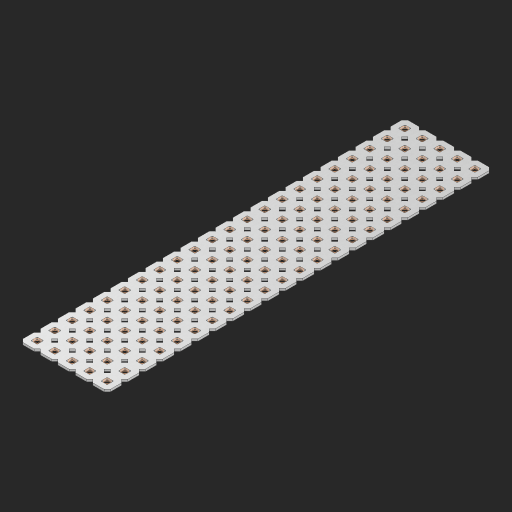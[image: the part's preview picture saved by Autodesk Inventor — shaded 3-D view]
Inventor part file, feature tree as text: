
AUTODESK INVENTOR PART (.ipt)
format: ipt  version: 2023 (Build 270158000, 158)  size: 1,554,432 bytes
history: native  units: in
note: dims shown in document units (in); Inventor stores cm internally (conversion verified against a paired STEP export)
features: other x111, extrude x109, sketch x2, pattern_linear x1
ambient origin geometry x8: Origin, YZ Plane, XZ Plane, XY Plane, X Axis, Y Axis, Z Axis, Center Point
bodies: Solid1 (feature_tree), Body (feature_tree)
feature tree (223):
  pattern_linear  "Rectangular Pattern1"  Spacing1=0.09in  [1 undecoded]
  sketch  "Sketch1"  dims[d1=0.5in]
  sketch  "Sketch2"  dims[d2=0.182in d3=0.09in d4=0.09in d5=0.09in d6=0.09in d7=0.09in d8=0.09in d9=0.09in d10=0.09in d11=0.02in d13=0.0in d14=0.172in d15=0.0625in d16=0.0in d19=0.5in d22=0.5in]
  other  "Srf1"
  other  "Srf126"
  other  "Srf127"
  other  "Srf128"
  other  "Srf129"
  other  "Srf130"
  other  "Srf131"
  other  "Srf250"
  other  "Srf251"
  other  "Srf252"
  other  "Srf253"
  other  "Srf254"
  other  "Srf255"
  other  "Srf256"
  other  "Srf257"
  other  "Srf258"
  other  "Srf259"
  other  "Srf260"
  other  "Srf261"
  other  "Srf262"
  other  "Srf263"
  other  "Srf264"
  other  "Srf268"
  other  "Srf269"
  other  "Srf270"
  other  "Srf271"
  other  "Srf272"
  other  "Srf273"
  other  "Srf274"
  other  "Srf275"
  other  "Srf276"
  other  "Srf277"
  other  "Srf278"
  other  "Srf279"
  other  "Srf280"
  other  "Srf281"
  other  "Srf282"
  other  "Srf283"
  other  "Srf284"
  other  "Srf285"
  other  "Srf286"
  other  "Srf287"
  other  "Srf288"
  other  "Srf289"
  other  "Srf293"
  other  "Srf294"
  other  "Srf295"
  other  "Srf296"
  other  "Srf297"
  other  "Srf298"
  other  "Srf299"
  other  "Srf300"
  other  "Srf301"
  other  "Srf302"
  other  "Srf303"
  other  "Srf304"
  other  "Srf305"
  other  "Srf306"
  other  "Srf307"
  other  "Srf308"
  other  "Srf309"
  other  "Srf310"
  other  "Srf311"
  other  "Srf312"
  other  "Srf313"
  other  "Srf314"
  other  "Srf318"
  other  "Srf319"
  other  "Srf320"
  other  "Srf321"
  other  "Srf322"
  other  "Srf323"
  other  "Srf324"
  other  "Srf325"
  other  "Srf326"
  other  "Srf327"
  other  "Srf328"
  other  "Srf329"
  other  "Srf330"
  other  "Srf331"
  other  "Srf332"
  other  "Srf333"
  other  "Srf334"
  other  "Srf335"
  other  "Srf336"
  other  "Srf337"
  other  "Srf338"
  other  "Srf339"
  other  "Srf343"
  other  "Srf344"
  other  "Srf345"
  other  "Srf346"
  other  "Srf347"
  other  "Srf348"
  other  "Srf349"
  other  "Srf350"
  other  "Srf351"
  other  "Srf352"
  other  "Srf353"
  other  "Srf354"
  other  "Srf355"
  other  "Srf356"
  other  "Srf357"
  other  "Srf358"
  other  "Srf359"
  other  "Srf360"
  other  "Srf361"
  other  "Srf362"
  other  "Srf363"
  other  "Srf364"
  other  "Circle"
  extrude  "ExtrusionSrf126"  Depth=0.09in
  extrude  "ExtrusionSrf127"  Depth=0.09in
  extrude  "ExtrusionSrf128"  Depth=0.09in
  extrude  "ExtrusionSrf129"  Depth=0.09in
  extrude  "ExtrusionSrf130"  Depth=0.09in
  extrude  "ExtrusionSrf131"  Depth=0.09in
  extrude  "ExtrusionSrf250"  Depth=0.09in
  extrude  "ExtrusionSrf251"  Depth=0.02in
  extrude  "ExtrusionSrf252"  TaperAngle=0.0deg  [1 undecoded]
  extrude  "ExtrusionSrf253"  Depth=0.5in
  extrude  "ExtrusionSrf254"  Depth=0.0625in TaperAngle=0.0deg
  extrude  "ExtrusionSrf255"  Depth=0.5in
  extrude  "ExtrusionSrf256"  Depth=0.5in
  extrude  "ExtrusionSrf257"  [1 undecoded]
  extrude  "ExtrusionSrf258"  [1 undecoded]
  extrude  "ExtrusionSrf259"  [1 undecoded]
  extrude  "ExtrusionSrf260"  [1 undecoded]
  extrude  "ExtrusionSrf261"  [1 undecoded]
  extrude  "ExtrusionSrf262"  [1 undecoded]
  extrude  "ExtrusionSrf263"  [1 undecoded]
  extrude  "ExtrusionSrf264"  [1 undecoded]
  extrude  "ExtrusionSrf268"  [1 undecoded]
  extrude  "ExtrusionSrf269"  [1 undecoded]
  extrude  "ExtrusionSrf270"  [1 undecoded]
  extrude  "ExtrusionSrf271"  [1 undecoded]
  extrude  "ExtrusionSrf272"  [1 undecoded]
  extrude  "ExtrusionSrf273"  [1 undecoded]
  extrude  "ExtrusionSrf274"  [1 undecoded]
  extrude  "ExtrusionSrf275"  [1 undecoded]
  extrude  "ExtrusionSrf276"  [1 undecoded]
  extrude  "ExtrusionSrf277"  [1 undecoded]
  extrude  "ExtrusionSrf278"  [1 undecoded]
  extrude  "ExtrusionSrf279"  [1 undecoded]
  extrude  "ExtrusionSrf280"  [1 undecoded]
  extrude  "ExtrusionSrf281"  [1 undecoded]
  extrude  "ExtrusionSrf282"  [1 undecoded]
  extrude  "ExtrusionSrf283"  [1 undecoded]
  extrude  "ExtrusionSrf284"  [1 undecoded]
  extrude  "ExtrusionSrf285"  [1 undecoded]
  extrude  "ExtrusionSrf286"  [1 undecoded]
  extrude  "ExtrusionSrf287"  [1 undecoded]
  extrude  "ExtrusionSrf288"  [1 undecoded]
  extrude  "ExtrusionSrf289"  [1 undecoded]
  extrude  "ExtrusionSrf293"  [1 undecoded]
  extrude  "ExtrusionSrf294"  [1 undecoded]
  extrude  "ExtrusionSrf295"  [1 undecoded]
  extrude  "ExtrusionSrf296"  [1 undecoded]
  extrude  "ExtrusionSrf297"  [1 undecoded]
  extrude  "ExtrusionSrf298"  [1 undecoded]
  extrude  "ExtrusionSrf299"  [1 undecoded]
  extrude  "ExtrusionSrf300"  [1 undecoded]
  extrude  "ExtrusionSrf301"  [1 undecoded]
  extrude  "ExtrusionSrf302"  [1 undecoded]
  extrude  "ExtrusionSrf303"  [1 undecoded]
  extrude  "ExtrusionSrf304"  [1 undecoded]
  extrude  "ExtrusionSrf305"  [1 undecoded]
  extrude  "ExtrusionSrf306"  [1 undecoded]
  extrude  "ExtrusionSrf307"  [1 undecoded]
  extrude  "ExtrusionSrf308"  [1 undecoded]
  extrude  "ExtrusionSrf309"  [1 undecoded]
  extrude  "ExtrusionSrf310"  [1 undecoded]
  extrude  "ExtrusionSrf311"  [1 undecoded]
  extrude  "ExtrusionSrf312"  [1 undecoded]
  extrude  "ExtrusionSrf313"  [1 undecoded]
  extrude  "ExtrusionSrf314"  [1 undecoded]
  extrude  "ExtrusionSrf318"  [1 undecoded]
  extrude  "ExtrusionSrf319"  [1 undecoded]
  extrude  "ExtrusionSrf320"  [1 undecoded]
  extrude  "ExtrusionSrf321"  [1 undecoded]
  extrude  "ExtrusionSrf322"  [1 undecoded]
  extrude  "ExtrusionSrf323"  [1 undecoded]
  extrude  "ExtrusionSrf324"  [1 undecoded]
  extrude  "ExtrusionSrf325"  [1 undecoded]
  extrude  "ExtrusionSrf326"  [1 undecoded]
  extrude  "ExtrusionSrf327"  [1 undecoded]
  extrude  "ExtrusionSrf328"  [1 undecoded]
  extrude  "ExtrusionSrf329"  [1 undecoded]
  extrude  "ExtrusionSrf330"  [1 undecoded]
  extrude  "ExtrusionSrf331"  [1 undecoded]
  extrude  "ExtrusionSrf332"  [1 undecoded]
  extrude  "ExtrusionSrf333"  [1 undecoded]
  extrude  "ExtrusionSrf334"  [1 undecoded]
  extrude  "ExtrusionSrf335"  [1 undecoded]
  extrude  "ExtrusionSrf336"  [1 undecoded]
  extrude  "ExtrusionSrf337"  [1 undecoded]
  extrude  "ExtrusionSrf338"  [1 undecoded]
  extrude  "ExtrusionSrf339"  [1 undecoded]
  extrude  "ExtrusionSrf343"  [1 undecoded]
  extrude  "ExtrusionSrf344"  [1 undecoded]
  extrude  "ExtrusionSrf345"  [1 undecoded]
  extrude  "ExtrusionSrf346"  [1 undecoded]
  extrude  "ExtrusionSrf347"  [1 undecoded]
  extrude  "ExtrusionSrf348"  [1 undecoded]
  extrude  "ExtrusionSrf349"  [1 undecoded]
  extrude  "ExtrusionSrf350"  [1 undecoded]
  extrude  "ExtrusionSrf351"  [1 undecoded]
  extrude  "ExtrusionSrf352"  [1 undecoded]
  extrude  "ExtrusionSrf353"  [1 undecoded]
  extrude  "ExtrusionSrf354"  [1 undecoded]
  extrude  "ExtrusionSrf355"  [1 undecoded]
  extrude  "ExtrusionSrf356"  [1 undecoded]
  extrude  "ExtrusionSrf357"  [1 undecoded]
  extrude  "ExtrusionSrf358"  [1 undecoded]
  extrude  "ExtrusionSrf359"  [1 undecoded]
  extrude  "ExtrusionSrf360"  [1 undecoded]
  extrude  "ExtrusionSrf361"  [1 undecoded]
  extrude  "ExtrusionSrf362"  [1 undecoded]
  extrude  "ExtrusionSrf363"  [1 undecoded]
  extrude  "ExtrusionSrf364"  [1 undecoded]
note: 98 required parameter values undecoded (feature->parameter linkage not recoverable at this tier; creation-order binding heuristic only, values carry confidence <= 0.55)
